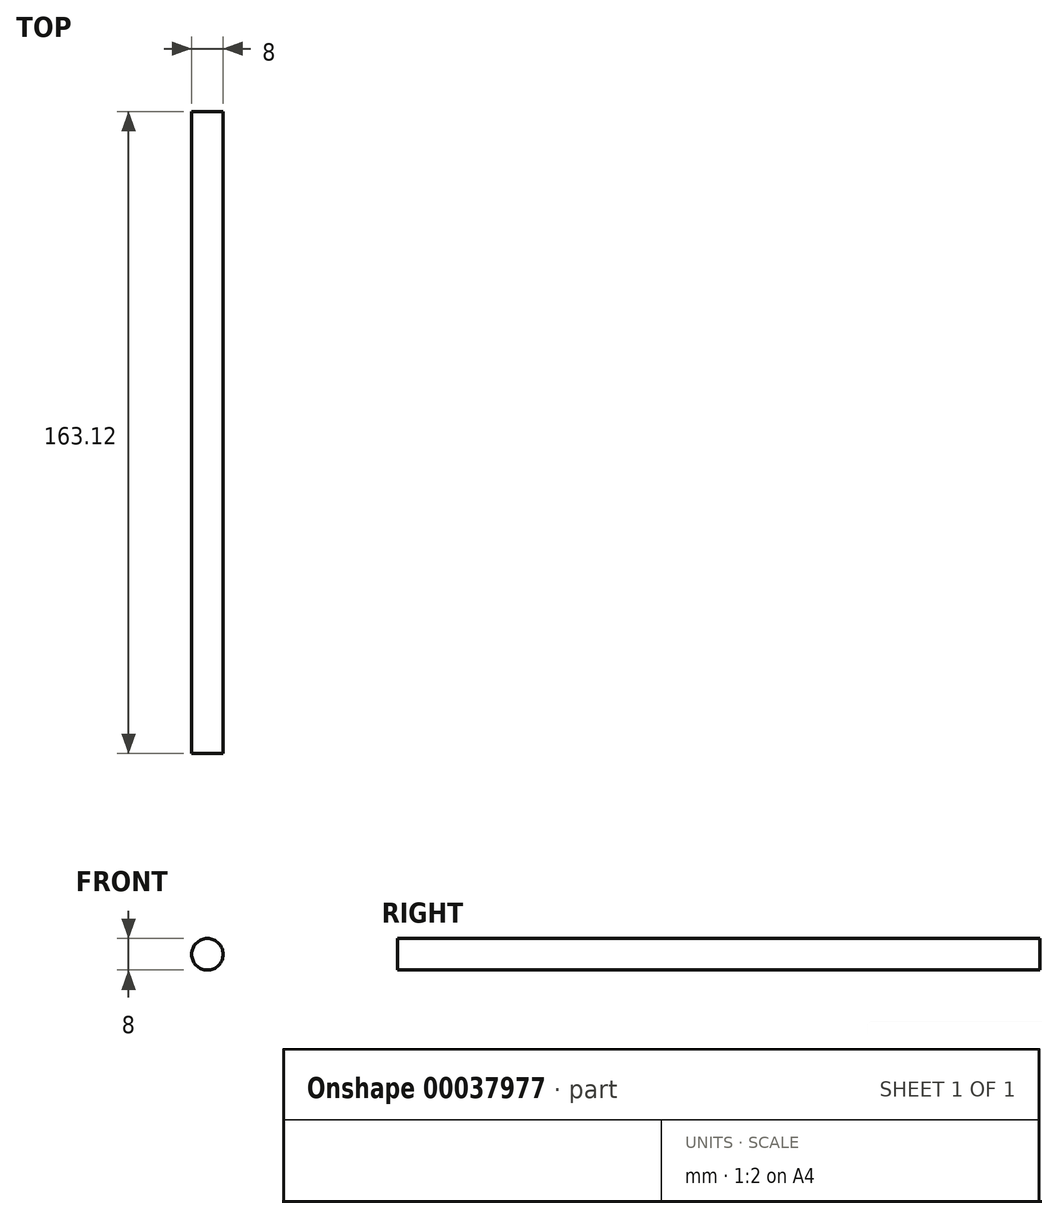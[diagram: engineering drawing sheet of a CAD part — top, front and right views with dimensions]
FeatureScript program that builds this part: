
annotation { "Feature Type Name" : "Feature", "Feature Type Description" : "" }
export const myFeature = defineFeature(function(context is Context, id is Id, definition is map)
    precondition{}
    {
        {
            var Q0;
            Q0=qCreatedBy(makeId("Front.planeOp"),FACE);
            var sketch = newSketch(context, id + "F0", { "sketchPlane" : qUnion([Q0])});
            skCircle(sketch, "E0", {"center": v(0, 0) * mm, "radius": 4 * mm});
            skSolve(sketch);
        }
        {
            var Q0;
            Q0=qSketchRegion(id+"F0",true);
            extrude(context, id + "F1", {"entities" : qUnion([Q0]), "depth" : 163.12 * mm});
        }
    });
